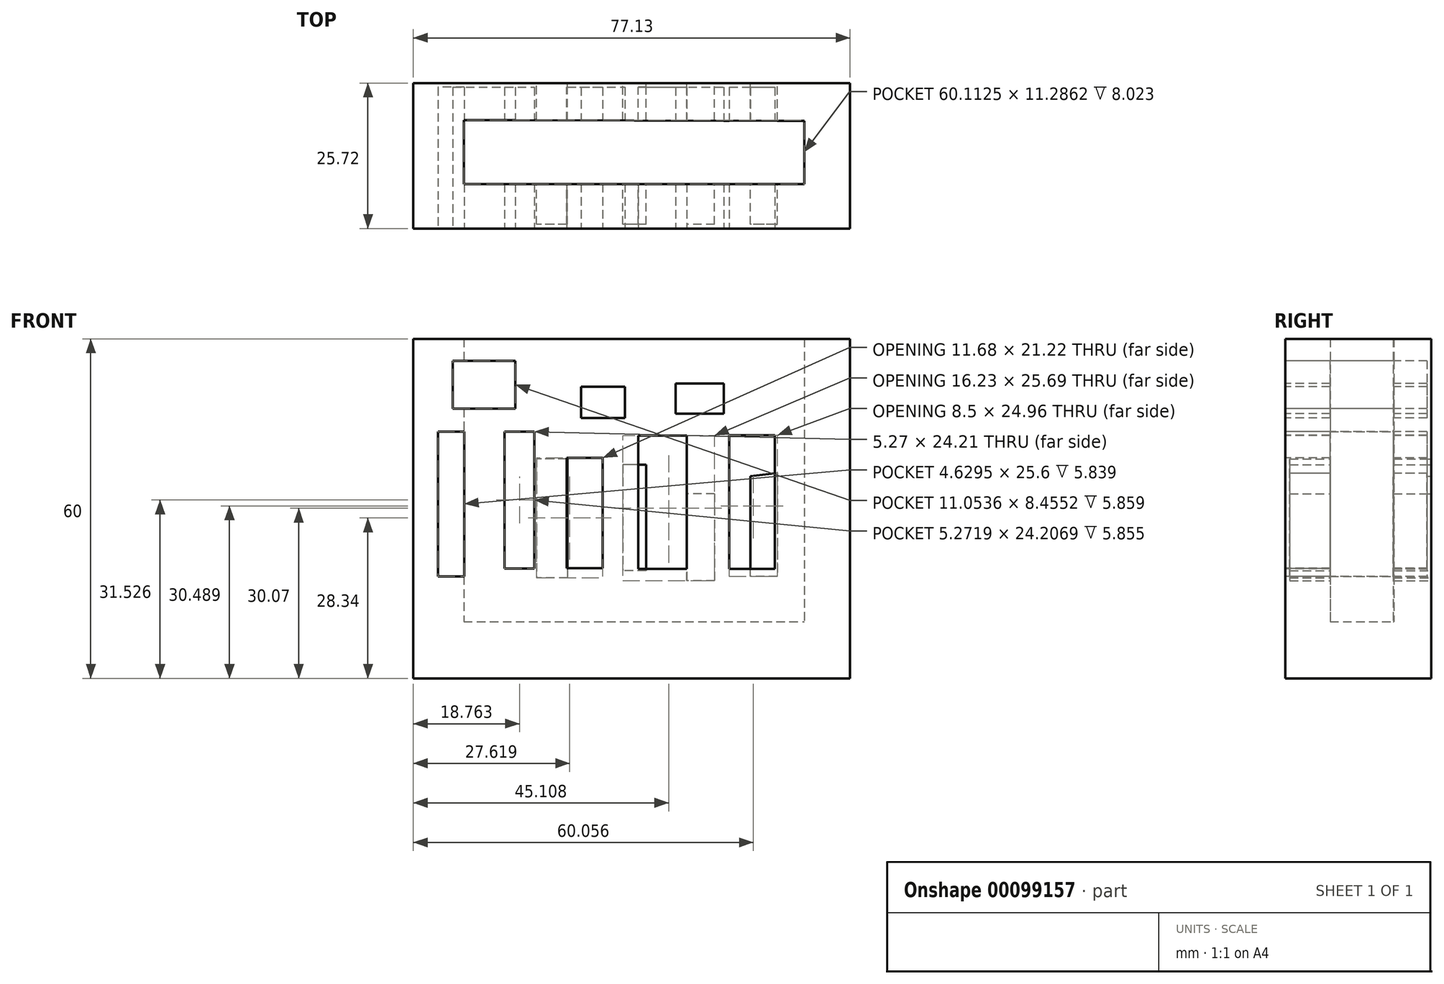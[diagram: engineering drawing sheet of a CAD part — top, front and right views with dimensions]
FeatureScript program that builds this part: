
annotation { "Feature Type Name" : "Feature", "Feature Type Description" : "" }
export const myFeature = defineFeature(function(context is Context, id is Id, definition is map)
    precondition{}
    {
        {
            var Q0;
            Q0=qCreatedBy(makeId("Top.planeOp"),FACE);
            var sketch = newSketch(context, id + "F0", { "sketchPlane" : qUnion([Q0])});
            skLineSegment(sketch, "E0", {"start": v(-39.38, -17.85) * mm, "end": v(20.74, -17.85) * mm});
            skLineSegment(sketch, "E1", {"start": v(-39.38, -17.85) * mm, "end": v(-39.38, -6.56) * mm});
            skLineSegment(sketch, "E2", {"start": v(20.74, -17.85) * mm, "end": v(20.74, -6.7) * mm});
            skLineSegment(sketch, "E3", {"start": v(20.74, -6.7) * mm, "end": v(-39.38, -6.56) * mm});
            skLineSegment(sketch, "E4", {"start": v(-48.3, -17.85) * mm, "end": v(-48.3, -6.56) * mm});
            skLineSegment(sketch, "E5", {"start": v(-48.3, -17.85) * mm, "end": v(-48.3, -25.72) * mm});
            skLineSegment(sketch, "E6", {"start": v(-48.3, -25.72) * mm, "end": v(28.83, -25.72) * mm});
            skLineSegment(sketch, "E7", {"start": v(28.83, -25.72) * mm, "end": v(28.83, 0) * mm});
            skLineSegment(sketch, "E8", {"start": v(-48.3, -6.56) * mm, "end": v(-48.3, 0) * mm});
            skLineSegment(sketch, "E9", {"start": v(-48.3, 0) * mm, "end": v(28.83, 0) * mm});
            skSolve(sketch);
        }
        {
            var Q0;
            Q0 = qSketchRegion(id + "F0", true);
            extrude(context, id + "F1", {"entities" : qUnion([Q0]), "depth" : 60 * mm});
        }
        {
            var Q0;
            Q0=makeQuery(id+"F0.imprint","IMPRINT",FACE,{"disambiguationData":[TD([[makeQuery(id+"F0.imprint","IMPRINT",EDGE,{"derivedFrom":sQuery(id+"F0.wireOp",EDGE,"E0")}),-1.0]])]});
            var sketch = newSketch(context, id + "F2", { "sketchPlane" : qUnion([Q0])});
            skSolve(sketch);
        }
        {
            var Q0;
            Q0=makeQuery(id+"F2.imprint","IMPRINT",FACE,{"disambiguationData":[TD([[makeQuery(id+"F2.imprint","IMPRINT",EDGE,{"derivedFrom":makeQuery(id+"F0.imprint","IMPRINT",EDGE,{"derivedFrom":sQuery(id+"F0.wireOp",EDGE,"E0")})}),1.0]])]});
            extrude(context, id + "F3", {"entities" : qUnion([Q0]), "operationType" : NewBodyOperationType.ADD, "depth" : 10 * mm});
        }
        {
            var Q0;
            Q0=makeQuery(id+"F1.opExtrude","SWEPT_FACE",FACE,{"disambiguationData":[OSD([sQuery(id+"F0.wireOp",EDGE,"E9")])]});
            var sketch = newSketch(context, id + "F4", { "sketchPlane" : qUnion([Q0])});
            skLineSegment(sketch, "E10", {"start": v(-16, 36.32) * mm, "end": v(-16, 18) * mm});
            skLineSegment(sketch, "E11", {"start": v(-16, 18) * mm, "end": v(-11.24, 18) * mm});
            skLineSegment(sketch, "E12", {"start": v(-11.24, 18) * mm, "end": v(-11.24, 35.74) * mm});
            skLineSegment(sketch, "E13", {"start": v(-11.24, 35.74) * mm, "end": v(-16, 36.32) * mm});
            skSolve(sketch);
        }
        {
            var Q0;
            Q0 = qSketchRegion(id + "F4", true);
            extrude(context, id + "F5", {"entities" : qUnion([Q0]), "operationType" : NewBodyOperationType.REMOVE, "oppositeDirection" : true, "depth" : 25 * mm});
        }
        {
            var Q0;
            Q0=makeQuery(id+"F1.opExtrude","SWEPT_FACE",FACE,{"disambiguationData":[OSD([sQuery(id+"F0.wireOp",EDGE,"E9")])]});
            var sketch = newSketch(context, id + "F6", { "sketchPlane" : qUnion([Q0])});
            skLineSegment(sketch, "E14.bottom", {"start": v(7.19, 37.76) * mm, "end": v(11.3, 37.76) * mm});
            skLineSegment(sketch, "E14.top", {"start": v(7.19, 19.03) * mm, "end": v(11.3, 19.03) * mm});
            skLineSegment(sketch, "E14.left", {"start": v(7.19, 37.76) * mm, "end": v(7.19, 19.03) * mm});
            skLineSegment(sketch, "E14.right", {"start": v(11.3, 37.76) * mm, "end": v(11.3, 19.03) * mm});
            skLineSegment(sketch, "E15.bottom", {"start": v(21.06, 38.8) * mm, "end": v(26.52, 38.8) * mm});
            skLineSegment(sketch, "E15.top", {"start": v(21.06, 17.73) * mm, "end": v(26.52, 17.73) * mm});
            skLineSegment(sketch, "E15.left", {"start": v(21.06, 38.8) * mm, "end": v(21.06, 17.73) * mm});
            skLineSegment(sketch, "E15.right", {"start": v(26.52, 38.8) * mm, "end": v(26.52, 17.73) * mm});
            skLineSegment(sketch, "E16.bottom", {"start": v(-4.92, 32.63) * mm, "end": v(0, 32.63) * mm});
            skLineSegment(sketch, "E16.top", {"start": v(-4.92, 17.23) * mm, "end": v(0, 17.23) * mm});
            skLineSegment(sketch, "E16.left", {"start": v(-4.92, 32.63) * mm, "end": v(-4.92, 17.23) * mm});
            skLineSegment(sketch, "E16.right", {"start": v(0, 32.63) * mm, "end": v(0, 17.23) * mm});
            skSolve(sketch);
        }
        {
            var Q0;
            Q0 = qSketchRegion(id + "F6", true);
            extrude(context, id + "F7", {"entities" : qUnion([Q0]), "operationType" : NewBodyOperationType.REMOVE, "oppositeDirection" : true, "depth" : 25 * mm});
        }
        {
            var Q0;
            Q0=makeQuery(id+"F1.opExtrude","SWEPT_FACE",FACE,{"disambiguationData":[OSD([sQuery(id+"F0.wireOp",EDGE,"E6")])]});
            var sketch = newSketch(context, id + "F8", { "sketchPlane" : qUnion([Q0])});
            skLineSegment(sketch, "E17.bottom", {"start": v(-32.17, 43.63) * mm, "end": v(-26.9, 43.63) * mm});
            skLineSegment(sketch, "E17.top", {"start": v(-32.17, 19.42) * mm, "end": v(-26.9, 19.42) * mm});
            skLineSegment(sketch, "E17.left", {"start": v(-32.17, 43.63) * mm, "end": v(-32.17, 19.42) * mm});
            skLineSegment(sketch, "E17.right", {"start": v(-26.9, 43.63) * mm, "end": v(-26.9, 19.42) * mm});
            skLineSegment(sketch, "E18.bottom", {"start": v(-21.23, 38.95) * mm, "end": v(-14.84, 38.95) * mm});
            skLineSegment(sketch, "E18.top", {"start": v(-21.23, 19.49) * mm, "end": v(-14.84, 19.49) * mm});
            skLineSegment(sketch, "E18.left", {"start": v(-21.23, 38.95) * mm, "end": v(-21.23, 19.49) * mm});
            skLineSegment(sketch, "E18.right", {"start": v(-14.84, 38.95) * mm, "end": v(-14.84, 19.49) * mm});
            skLineSegment(sketch, "E19.bottom", {"start": v(-8.59, 42.91) * mm, "end": v(0, 42.91) * mm});
            skLineSegment(sketch, "E19.top", {"start": v(-8.59, 19.32) * mm, "end": v(0, 19.32) * mm});
            skLineSegment(sketch, "E19.left", {"start": v(-8.59, 42.91) * mm, "end": v(-8.59, 19.32) * mm});
            skLineSegment(sketch, "E19.right", {"start": v(0, 42.91) * mm, "end": v(0, 19.32) * mm});
            skLineSegment(sketch, "E20.bottom", {"start": v(7.5, 42.97) * mm, "end": v(15.54, 42.97) * mm});
            skLineSegment(sketch, "E20.top", {"start": v(7.5, 19.35) * mm, "end": v(15.54, 19.35) * mm});
            skLineSegment(sketch, "E20.left", {"start": v(7.5, 42.97) * mm, "end": v(7.5, 19.35) * mm});
            skLineSegment(sketch, "E20.right", {"start": v(15.54, 42.97) * mm, "end": v(15.54, 19.35) * mm});
            skLineSegment(sketch, "E21.bottom", {"start": v(-39.3, 43.62) * mm, "end": v(-43.92, 43.62) * mm});
            skLineSegment(sketch, "E21.top", {"start": v(-39.3, 18.02) * mm, "end": v(-43.92, 18.02) * mm});
            skLineSegment(sketch, "E21.left", {"start": v(-39.3, 43.62) * mm, "end": v(-39.3, 18.02) * mm});
            skLineSegment(sketch, "E21.right", {"start": v(-43.92, 43.62) * mm, "end": v(-43.92, 18.02) * mm});
            skLineSegment(sketch, "E22.bottom", {"start": v(-18.67, 51.55) * mm, "end": v(-10.9, 51.55) * mm});
            skLineSegment(sketch, "E22.top", {"start": v(-18.67, 46.02) * mm, "end": v(-10.9, 46.02) * mm});
            skLineSegment(sketch, "E22.left", {"start": v(-18.67, 51.55) * mm, "end": v(-18.67, 46.02) * mm});
            skLineSegment(sketch, "E22.right", {"start": v(-10.9, 51.55) * mm, "end": v(-10.9, 46.02) * mm});
            skLineSegment(sketch, "E23.bottom", {"start": v(-2, 52.14) * mm, "end": v(6.55, 52.14) * mm});
            skLineSegment(sketch, "E23.top", {"start": v(-2, 46.81) * mm, "end": v(6.55, 46.81) * mm});
            skLineSegment(sketch, "E23.left", {"start": v(-2, 52.14) * mm, "end": v(-2, 46.81) * mm});
            skLineSegment(sketch, "E23.right", {"start": v(6.55, 52.14) * mm, "end": v(6.55, 46.81) * mm});
            skLineSegment(sketch, "E24.bottom", {"start": v(-41.32, 56.13) * mm, "end": v(-30.26, 56.13) * mm});
            skLineSegment(sketch, "E24.top", {"start": v(-41.32, 47.67) * mm, "end": v(-30.26, 47.67) * mm});
            skLineSegment(sketch, "E24.left", {"start": v(-41.32, 56.13) * mm, "end": v(-41.32, 47.67) * mm});
            skLineSegment(sketch, "E24.right", {"start": v(-30.26, 56.13) * mm, "end": v(-30.26, 47.67) * mm});
            skSolve(sketch);
        }
        {
            var Q0;
            Q0=makeQuery(id+"F8.imprint","IMPRINT",FACE,{"disambiguationData":[TD([[makeQuery(id+"F8.imprint","IMPRINT",EDGE,{"derivedFrom":sQuery(id+"F8.wireOp",EDGE,"E17.bottom")}),-1.0]])]});
            var Q1;
            Q1=makeQuery(id+"F8.imprint","IMPRINT",FACE,{"disambiguationData":[TD([[makeQuery(id+"F8.imprint","IMPRINT",EDGE,{"derivedFrom":sQuery(id+"F8.wireOp",EDGE,"E18.bottom")}),-1.0]])]});
            var Q2;
            Q2=makeQuery(id+"F8.imprint","IMPRINT",FACE,{"disambiguationData":[TD([[makeQuery(id+"F8.imprint","IMPRINT",EDGE,{"derivedFrom":sQuery(id+"F8.wireOp",EDGE,"E19.bottom")}),-1.0]])]});
            var Q3;
            Q3=makeQuery(id+"F8.imprint","IMPRINT",FACE,{"disambiguationData":[TD([[makeQuery(id+"F8.imprint","IMPRINT",EDGE,{"derivedFrom":sQuery(id+"F8.wireOp",EDGE,"E20.bottom")}),-1.0]])]});
            var Q4;
            Q4=makeQuery(id+"F8.imprint","IMPRINT",FACE,{"disambiguationData":[TD([[makeQuery(id+"F8.imprint","IMPRINT",EDGE,{"derivedFrom":sQuery(id+"F8.wireOp",EDGE,"E21.bottom")}),1.0]])]});
            var Q5;
            Q5=makeQuery(id+"F8.imprint","IMPRINT",FACE,{"disambiguationData":[TD([[makeQuery(id+"F8.imprint","IMPRINT",EDGE,{"derivedFrom":sQuery(id+"F8.wireOp",EDGE,"E22.bottom")}),-1.0]])]});
            var Q6;
            Q6=makeQuery(id+"F8.imprint","IMPRINT",FACE,{"disambiguationData":[TD([[makeQuery(id+"F8.imprint","IMPRINT",EDGE,{"derivedFrom":sQuery(id+"F8.wireOp",EDGE,"E23.bottom")}),-1.0]])]});
            var Q7;
            Q7=makeQuery(id+"F8.imprint","IMPRINT",FACE,{"disambiguationData":[TD([[makeQuery(id+"F8.imprint","IMPRINT",EDGE,{"derivedFrom":sQuery(id+"F8.wireOp",EDGE,"E24.bottom")}),-1.0]])]});
            extrude(context, id + "F9", {"entities" : qUnion([Q0, Q1, Q2, Q3, Q4, Q5, Q6, Q7]), "operationType" : NewBodyOperationType.REMOVE, "oppositeDirection" : true, "depth" : 25 * mm});
        }
    });
